# Revit family: Thorn TONIC M
name_source: partatom
category: Lighting Fixtures
revit_build: Autodesk Revit 2018 (Build: 20170223_1515(x64)
units: mm (PartAtom-declared; Revit-internal decimal feet)

## family parameters
Cut with Voids When Loaded = No
Host = Face
Light Source = No
OmniClass Number = 23.80.70.11
OmniClass Title = Luminaries for Internal Lighting
Part Type = Normal
Room Calculation Point = No
Round Connector Dimension = Use Diameter
Shared = No

## types (1)
- TONIC M 3600 940  3GU FL BK
    Apparent Load = 31 VA
    Assembly Code = D5020200
    Body = ZG_Metal_Black
    Default Elevation = 0 mm  [stored 0 ft]
    Description = LED spot luminaires
    Height = 85 mm
    Lamp = LED
    Length = 150 mm
    Manufacturer = Thorn Lighting
    Model = 96638029
    Reflector = ZG_SI_Opaque
    URL = www.thornlighting.com//96638029
    Voltage = 230 V

note: [stored X ft] marks values corroborated as IEEE doubles in the binary element streams (Revit-internal decimal feet)

## geometry (parser evidence)
native form markers: Sweep x3
no freeform markers — native parametric forms only
